# Revit family: Base_Cabinets-Teknion-CEBDF_Base_Cabinet_Four_Drawers-R2022
name_source: partatom
category: Furniture
units: mm (PartAtom-declared; Revit-internal decimal feet)

## family parameters
Always vertical = Yes
Cut with Voids When Loaded = No
Enable Cutting in Views = No
OmniClass Number = 23.40.20.00
OmniClass Title = General Furniture and Specialties
Render Appearance Source = Family Geometry
Room Calculation Point = No
Shared = Yes
Work Plane-Based = No

## types (1)
- Equal Configuration
    Assembly Code = E2020200
    Default Elevation = 0 "
    Description = Base Cabinet - Four Drawers, Equal Configuration
    E - Equal = Yes
    Manufacturer = Teknion
    Manufacturer Fax = 416.661.4586
    Model = CEBDFE____
    Part Number = CEBDF
    Product Documentation Link = https://www.teknion.com
    Product Line = Base Cabinets
    Product Page URL = https://www.teknion.com
    Series = Expansion Casework+
    Sustainability Data = https://www.teknion.com
    URL = www.teknion.com
    Unit Weight URL = http://www.teknion.com
    Warranty = http://www.teknion.com

## geometry (parser evidence)
native form markers: Sweep x4
no freeform markers — native parametric forms only
